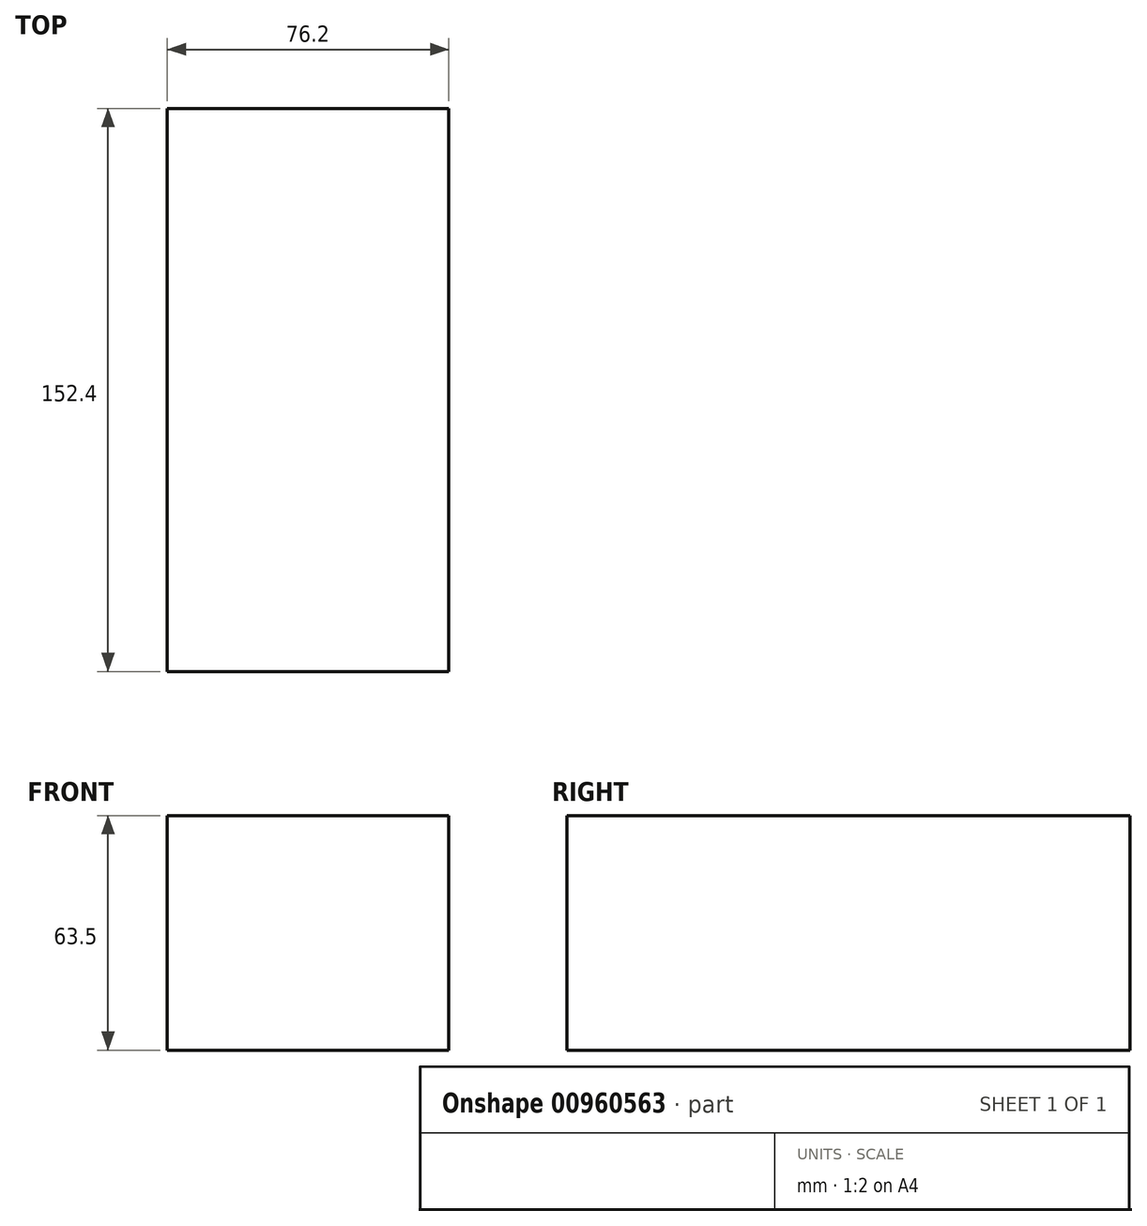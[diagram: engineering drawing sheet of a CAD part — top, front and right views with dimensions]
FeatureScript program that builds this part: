
annotation { "Feature Type Name" : "Feature", "Feature Type Description" : "" }
export const myFeature = defineFeature(function(context is Context, id is Id, definition is map)
    precondition{}
    {
        {
            var Q0;
            Q0=qCreatedBy(makeId("Top.planeOp"),FACE);
            var sketch = newSketch(context, id + "F0", { "sketchPlane" : qUnion([Q0])});
            skLineSegment(sketch, "E0.bottom", {"start": v(19.05, -45.43) * mm, "end": v(-57.15, -45.43) * mm});
            skLineSegment(sketch, "E0.top", {"start": v(19.05, 106.97) * mm, "end": v(-57.15, 106.97) * mm});
            skLineSegment(sketch, "E0.left", {"start": v(19.05, -45.43) * mm, "end": v(19.05, 106.97) * mm});
            skLineSegment(sketch, "E0.right", {"start": v(-57.15, -45.43) * mm, "end": v(-57.15, 106.97) * mm});
            skPoint(sketch, "E0.middle", {"position": v(-19.05, 30.77) * mm});
            skSolve(sketch);
        }
        {
            var Q0;
            Q0=makeQuery(id+"F0.imprint","IMPRINT",FACE,{"disambiguationData":[TD([[makeQuery(id+"F0.imprint","IMPRINT",EDGE,{"derivedFrom":sQuery(id+"F0.wireOp",EDGE,"E0.bottom")}),-1.0]])]});
            extrude(context, id + "F1", {"entities" : qUnion([Q0]), "depth" : 63.5 * mm, "offsetDistance" : 25.4 * mm});
        }
    });
